# Revit family: IS_TonicII_Multiproduct_BIM_DE_A6330;A6331
name_source: partatom
category: Plumbing Fixtures
revit_build: Autodesk Revit 2015 (Build: 20140606_1530(x64)
units: mm (PartAtom-declared; Revit-internal decimal feet)

## types (2) — shared parameters
A6330 = Yes
AreaUnits = millimeters
Assembly Code = C1030200
AssetType = Fixed
Brand = Ideal Standard
ConnectionType = Plumbing
Default Elevation = 1219 mm
DurationUnit = year
ExpectedLife = 25
FaucetFunction = MIXED
FaucetOperation = Other
FaucetTopDescription = Lever
FaucetType = Other
Finish = Chrome
IfcExportAs = IfcValveType
IfcExportType = FAUCET
InstallationDate = 1900-12-31T23:59:59
InstallationInstructions = www.idealstandard.de\produkte
LinearUnits = millimeters
ManufacturerURL = www.idealstandard.com
NBSDescription = Water supply fitting for wash basins and troughs
NBSReference = 45-35-70/371
NominalDepth = 143 mm
NominalHeight = 137 mm
NominalLength = 143 mm
NominalWidth = 51 mm
ProductInformation = www.idealstandard.de/produkte
Shape = Sculptured
Size = 137 x 144 x 52 mm
Space = Internal
SpareParts = www.idealstandard.de/ersatzteile
TestPressure = 10 Bar
URL = www.idealstandard.com
Uniclass2015Code = Pr_40_20_87_98
Uniclass2015Title = Water supply fittings for wash basins and troughs
Uniclass2015Version = Products v1.1
Version = 1
VolumeUnits = Litres
WarrantyStartDate = 1900-12-31T23:59:59
WorkingPressure = 1-5 Bar

## per-type parameters (varying)
| type | BIMObjectName | BarCode | Description | Features | Model | ModelNumber | ModelReference | Name | NettWeight |
| A6330AA - | ISI_IdealStandard_WashBasinTaps_TonicII_A6330 | 4015413334976 | A6330AA TONIC II PICCOLO single lever one hole basin mixer with pop-up waste | TONIC II PICCOLO single lever one hole basin mixer with pop-up waste | A6330AA | A6330AA | Tonic ii single lever one hole small basin mixer with pop-up waste | WashBasinTaps_TonicII_A6330_IdealStandard | 1.7 Kg |
| A6331AA - | ISI_IdealStandard_WashBasinTaps_TonicII_A6331 | 4015413334983 | A6331AA TONIC II PICCOLO single lever one hole basin mixer, no pop-up waste | TONIC II PICCOLO single lever one hole basin mixer, no pop-up waste | A6331AA | A6331AA | Tonic ii single lever one hole small basin mixer without pop-up waste | WashBasinTaps_TonicII_A6331_IdealStandard | 1.3 Kg |

## geometry (parser evidence)
native form markers: Blend x2, Sweep x4
no freeform markers — native parametric forms only
